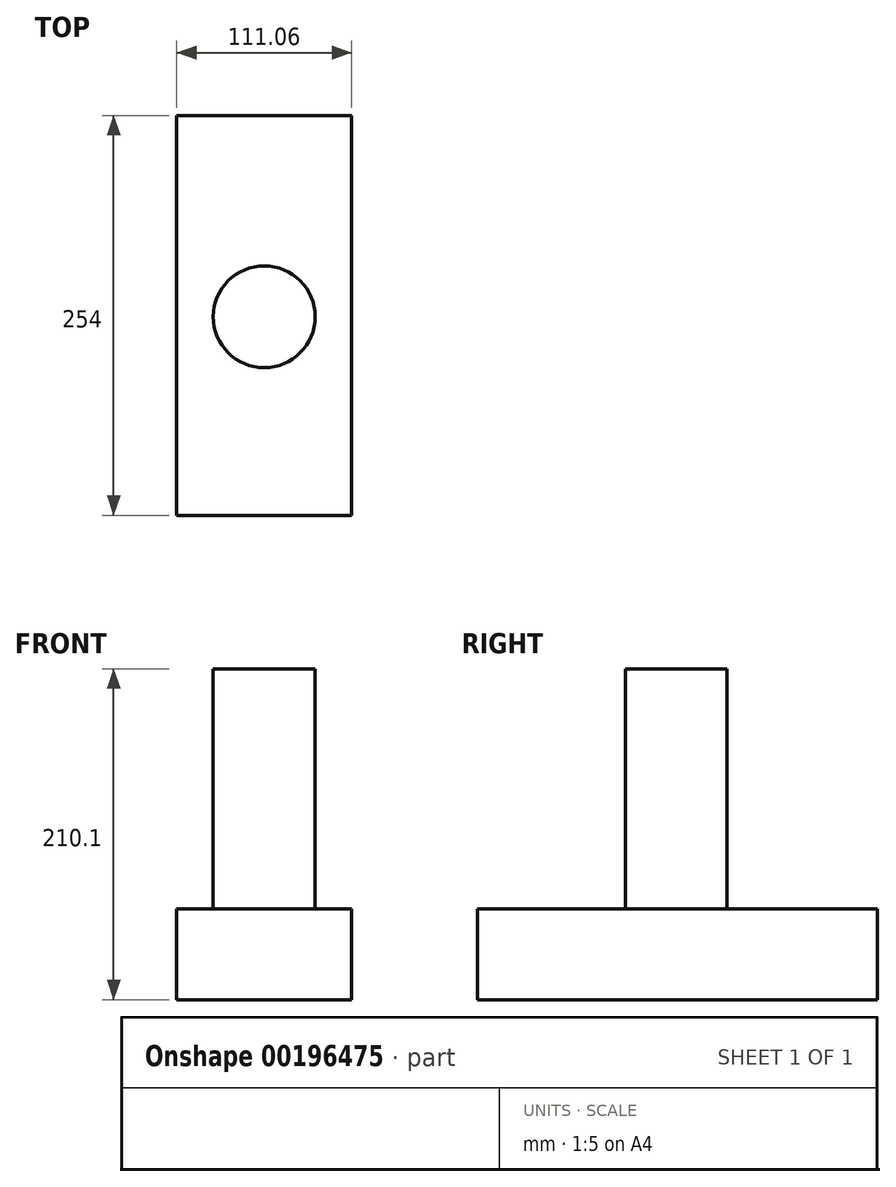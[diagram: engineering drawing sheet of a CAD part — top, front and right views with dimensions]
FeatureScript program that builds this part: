
annotation { "Feature Type Name" : "Feature", "Feature Type Description" : "" }
export const myFeature = defineFeature(function(context is Context, id is Id, definition is map)
    precondition{}
    {
        {
            var Q0;
            Q0=qCreatedBy(makeId("Front.planeOp"),FACE);
            var sketch = newSketch(context, id + "F0", { "sketchPlane" : qUnion([Q0])});
            skLineSegment(sketch, "E0.bottom", {"start": v(55.53, 28.85) * mm, "end": v(-55.53, 28.85) * mm});
            skLineSegment(sketch, "E0.top", {"start": v(55.53, -28.85) * mm, "end": v(-55.53, -28.85) * mm});
            skLineSegment(sketch, "E0.left", {"start": v(55.53, 28.85) * mm, "end": v(55.53, -28.85) * mm});
            skLineSegment(sketch, "E0.right", {"start": v(-55.53, 28.85) * mm, "end": v(-55.53, -28.85) * mm});
            skPoint(sketch, "E0.middle", {"position": v(0, 0) * mm});
            skSolve(sketch);
        }
        {
            var Q0;
            Q0=makeQuery(id+"F0.imprint","IMPRINT",FACE,{"disambiguationData":[TD([[makeQuery(id+"F0.imprint","IMPRINT",EDGE,{"derivedFrom":sQuery(id+"F0.wireOp",EDGE,"E0.bottom")}),1.0]])]});
            extrude(context, id + "F1", {"entities" : qUnion([Q0]), "depth" : 254 * mm});
        }
        {
            var Q0;
            Q0=makeQuery(id+"F1.opExtrude","SWEPT_FACE",FACE,{"disambiguationData":[OSD([sQuery(id+"F0.wireOp",EDGE,"E0.bottom")])]});
            var sketch = newSketch(context, id + "F2", { "sketchPlane" : qUnion([Q0])});
            skCircle(sketch, "E1", {"center": v(0, -127.83) * mm, "radius": 32.34 * mm});
            skSolve(sketch);
        }
        {
            var Q0;
            Q0=makeQuery(id+"F2.imprint","IMPRINT",FACE,{"disambiguationData":[TD([[makeQuery(id+"F2.imprint","IMPRINT",EDGE,{"derivedFrom":sQuery(id+"F2.wireOp",EDGE,"E1")}),1.0]])]});
            extrude(context, id + "F3", {"entities" : qUnion([Q0]), "operationType" : NewBodyOperationType.ADD, "depth" : 152.4 * mm});
        }
    });
